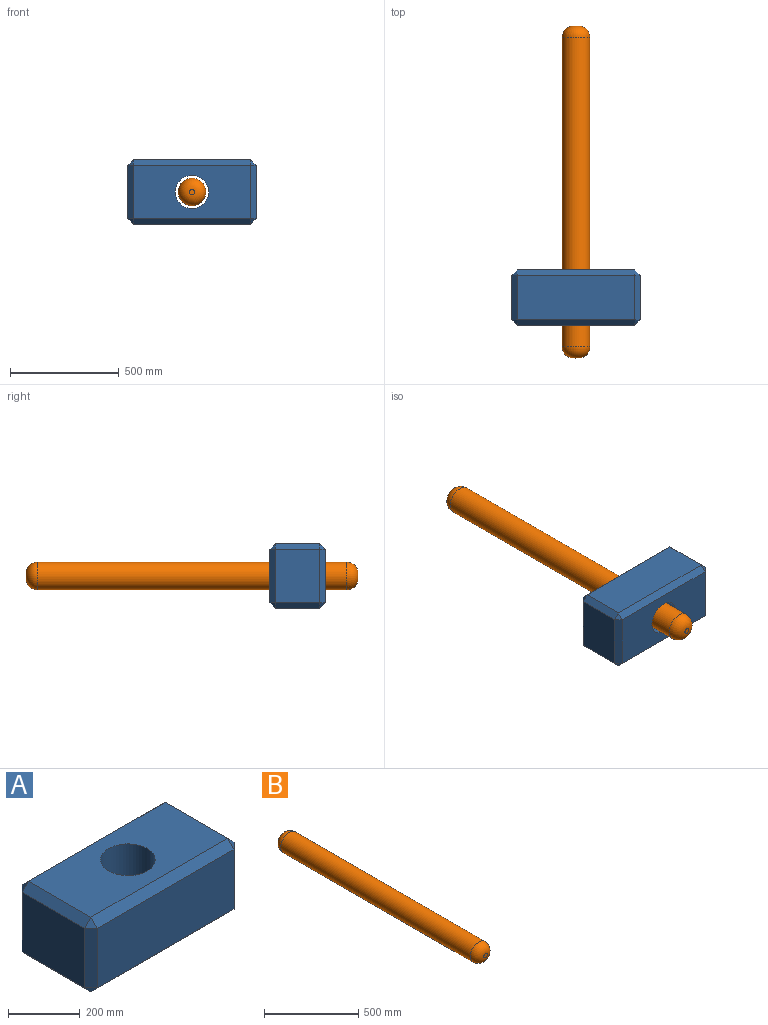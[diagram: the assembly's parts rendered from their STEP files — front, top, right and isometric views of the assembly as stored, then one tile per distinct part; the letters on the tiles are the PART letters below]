
ASSEMBLY  parts=2 mates=1
PART A: 27 faces, bbox 588.9x296.5x254 mm
  f0: plane 538.08x203.2mm, normal (0,-1,0), area 109337.6mm2, adj f13,f14,f22,f23
  f1: plane 245.71x203.2mm, normal (1,0,0), area 49928.9mm2, adj f7,f10,f14,f15
  f2: plane 538.08x203.2mm, normal (0,1,0), area 109337.6mm2, adj f10,f11,f20,f21
  f3: cylinder r=76.2mm len=254mm, axis (0,0,-1), area 121609.8mm2, adj f5,f6
  f4: plane 245.71x203.2mm, normal (-1,0,0), area 49928.9mm2, adj f12,f21,f22,f26
  f5: plane 538.08x245.71mm, normal (0,0,1), area 113971.5mm2, adj f3,f7,f11,f12,f13
  f6: plane 538.08x245.71mm, normal (0,0,-1), area 113971.5mm2, adj f3,f15,f20,f23,f26
  f7: plane 245.71x25.4mm, normal (0.71,0,0.71), area 8826.3mm2, adj f1,f5,f8,f9
  f8: plane 25.4x25.4mm, normal (0.58,0.58,0.58), area 558.7mm2, adj f7,f10,f11
  f9: plane 25.4x25.4mm, normal (0.58,-0.58,0.58), area 558.7mm2, adj f7,f13,f14
  f10: plane 203.2x25.4mm, normal (0.71,0.71,0), area 7299.2mm2, adj f1,f2,f8,f16
  f11: plane 538.08x25.4mm, normal (0,0.71,0.71), area 19328.3mm2, adj f2,f5,f8,f17
  f12: plane 245.71x25.4mm, normal (-0.71,0,0.71), area 8826.3mm2, adj f4,f5,f17,f18
  f13: plane 538.08x25.4mm, normal (0,-0.71,0.71), area 19328.3mm2, adj f0,f5,f9,f18
  f14: plane 203.2x25.4mm, normal (0.71,-0.71,0), area 7299.2mm2, adj f0,f1,f9,f19
  f15: plane 245.71x25.4mm, normal (0.71,0,-0.71), area 8826.3mm2, adj f1,f6,f16,f19
  f16: plane 25.4x25.4mm, normal (0.58,0.58,-0.58), area 558.7mm2, adj f10,f15,f20
  f17: plane 25.4x25.4mm, normal (-0.58,0.58,0.58), area 558.7mm2, adj f11,f12,f21
  f18: plane 25.4x25.4mm, normal (-0.58,-0.58,0.58), area 558.7mm2, adj f12,f13,f22
  f19: plane 25.4x25.4mm, normal (0.58,-0.58,-0.58), area 558.7mm2, adj f14,f15,f23
  f20: plane 538.08x25.4mm, normal (0,0.71,-0.71), area 19328.3mm2, adj f2,f6,f16,f24
  f21: plane 203.2x25.4mm, normal (-0.71,0.71,0), area 7299.2mm2, adj f2,f4,f17,f24
  f22: plane 203.2x25.4mm, normal (-0.71,-0.71,0), area 7299.2mm2, adj f0,f4,f18,f25
  f23: plane 538.08x25.4mm, normal (0,-0.71,-0.71), area 19328.3mm2, adj f0,f6,f19,f25
  f24: plane 25.4x25.4mm, normal (-0.58,0.58,-0.58), area 558.7mm2, adj f20,f21,f26
  f25: plane 25.4x25.4mm, normal (-0.58,-0.58,-0.58), area 558.7mm2, adj f22,f23,f26
  f26: plane 245.71x25.4mm, normal (-0.71,0,-0.71), area 8826.3mm2, adj f4,f6,f24,f25
PART B: 5 faces, bbox 127x1524x127 mm
  f0: cylinder r=63.5mm len=1422.4mm, axis (0,1,0), area 567512.4mm2, adj f3,f4
  f1: plane 25.4x25.4mm, normal (0,-1,0), area 506.7mm2, adj f4
  f2: plane 25.4x25.4mm, normal (0,1,0), area 506.7mm2, adj f3
  f3: torus R=12.7mm, axis (0,-1,0), area 22582.1mm2, adj f0,f2
  f4: torus R=12.7mm, axis (0,-1,0), area 22582.1mm2, adj f0,f1
PLACE A rot(axis=(1,0,0),90deg) t=(-1186.04,-2224.36,-2561.18)mm
PLACE B rot(axis=(0,-0.32,-0.95),0deg) t=(-1186.04,-1104.52,-2561.18)mm
MATE cylindrical A.f3 <-> B.f0  axis (0,1,0) through (-1186.04,-2478.36,-2561.18)mm
